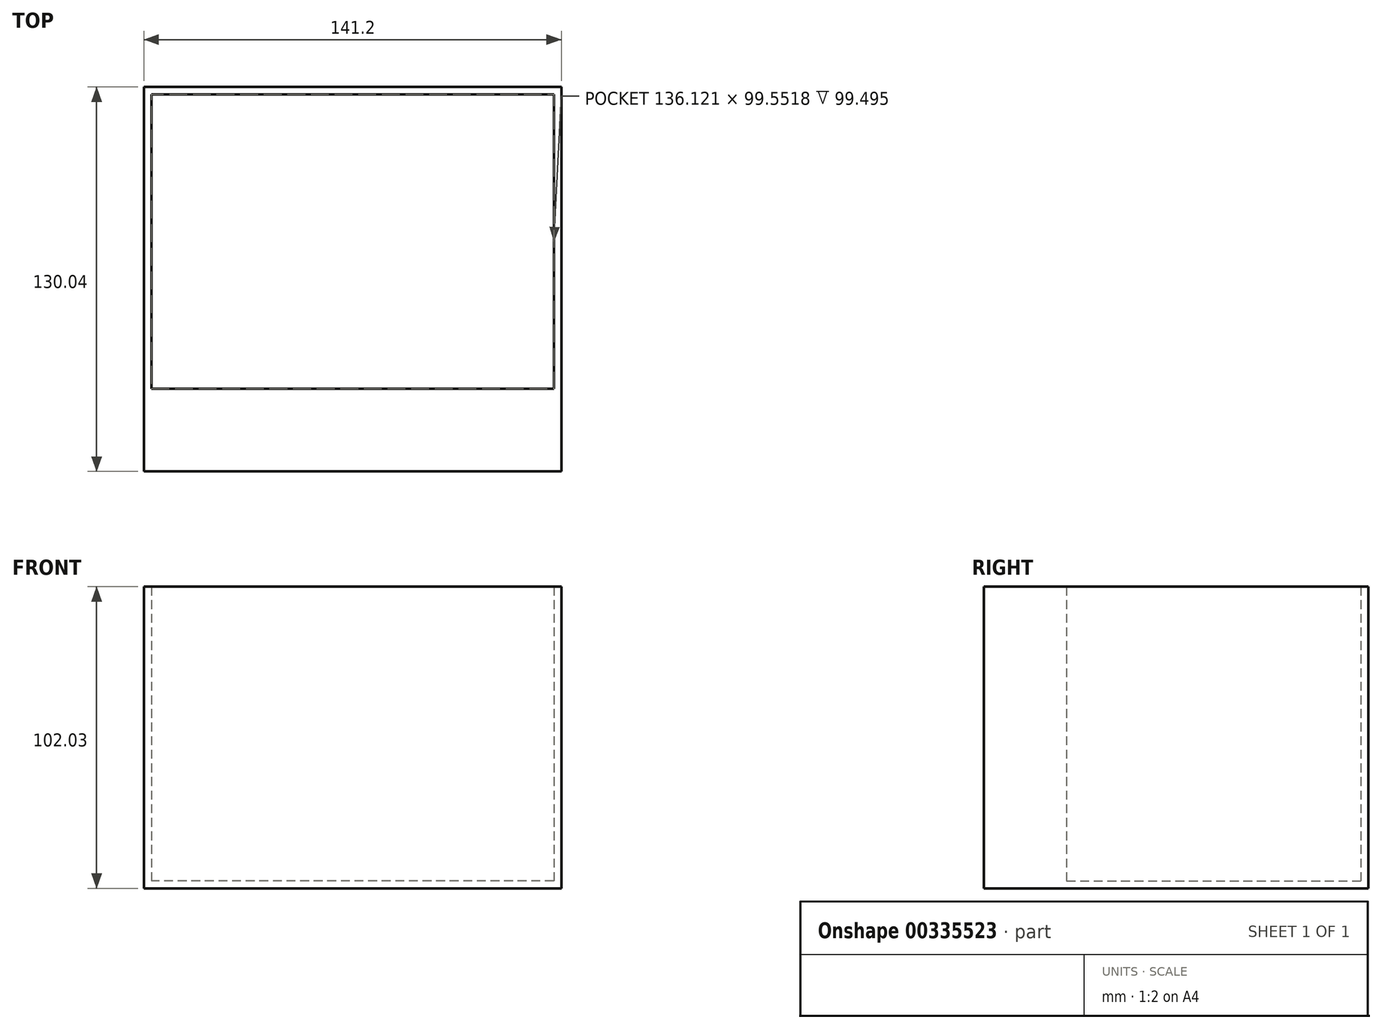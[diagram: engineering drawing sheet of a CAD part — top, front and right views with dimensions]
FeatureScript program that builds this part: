
annotation { "Feature Type Name" : "Feature", "Feature Type Description" : "" }
export const myFeature = defineFeature(function(context is Context, id is Id, definition is map)
    precondition{}
    {
        {
            var Q0;
            Q0=qCreatedBy(makeId("Top.planeOp"),FACE);
            var sketch = newSketch(context, id + "F0", { "sketchPlane" : qUnion([Q0])});
            skLineSegment(sketch, "E0.bottom", {"start": v(70.6, -52.32) * mm, "end": v(-70.6, -52.32) * mm});
            skLineSegment(sketch, "E0.top", {"start": v(70.6, 52.32) * mm, "end": v(-70.6, 52.32) * mm});
            skLineSegment(sketch, "E0.left", {"start": v(70.6, -52.32) * mm, "end": v(70.6, 52.32) * mm});
            skLineSegment(sketch, "E0.right", {"start": v(-70.6, -52.32) * mm, "end": v(-70.6, 52.32) * mm});
            skPoint(sketch, "E0.middle", {"position": v(0, 0) * mm});
            skSolve(sketch);
        }
        {
            var Q0;
            Q0=makeQuery(id+"F0.imprint","IMPRINT",FACE,{"disambiguationData":[TD([[makeQuery(id+"F0.imprint","IMPRINT",EDGE,{"derivedFrom":sQuery(id+"F0.wireOp",EDGE,"E0.bottom")}),-1.0]])]});
            var sketch = newSketch(context, id + "F1", { "sketchPlane" : qUnion([Q0])});
            skSolve(sketch);
        }
        {
            var Q0;
            Q0 = qSketchRegion(id + "F1", true);
            var Q1;
            Q1=makeQuery(id+"F1.imprint","IMPRINT",FACE,{"disambiguationData":[TD([[makeQuery(id+"F1.imprint","IMPRINT",EDGE,{"derivedFrom":makeQuery(id+"F0.imprint","IMPRINT",EDGE,{"derivedFrom":sQuery(id+"F0.wireOp",EDGE,"E0.bottom")})}),-1.0]])]});
            extrude(context, id + "F2", {"entities" : qUnion([Q0, Q1]), "depth" : 102.03 * mm});
        }
        {
            var Q0;
            Q0=makeQuery(id+"F2.opExtrude","CAP_FACE",FACE,{"disambiguationData":[OSD([sQuery(id+"F0.wireOp",EDGE,"E0.bottom"),sQuery(id+"F0.wireOp",EDGE,"E0.top"),sQuery(id+"F0.wireOp",EDGE,"E0.left"),sQuery(id+"F0.wireOp",EDGE,"E0.right")])],"isStart":false});
            shell(context, id + "F3", {"entities" : qUnion([Q0]), "thickness" : 2.54 * mm});
        }
        {
            var Q0;
            Q0=makeQuery(id+"F2.opExtrude","SWEPT_FACE",FACE,{"disambiguationData":[OSD([sQuery(id+"F0.wireOp",EDGE,"E0.bottom")])]});
            extrude(context, id + "F4", {"entities" : qUnion([Q0]), "operationType" : NewBodyOperationType.ADD, "depth" : 25.4 * mm});
        }
    });
